# Revit family: AluStar Rondo
name_source: partatom
category: HLS-Bauteile
revit_build: Autodesk Revit 2018 (Build: 20170223_1515(x64)
units: mm (PartAtom-declared; Revit-internal decimal feet)

## family parameters
Basisbauteil = Wand
Beim Laden mit Abzugskörper schneiden = Nein
Bemaßung runder Anschluss = Durchmesser verwenden
Gemeinsam genutzt = Nein
Immer vertikal = Ja
Raumberechnungspunkt = Nein
Teiletyp = Normal

## types (6) — shared parameters
Rohbauöffnung = Ja
T1 = 13.5 mm
T2 = 39 mm
T_plate = 1.5 mm  [stored 0.00492126 ft]

## per-type parameters (varying)
| type | B | B1 | B2_Max | B2_min | B3 | B4 | B5 | BLock | Binner | Bz | Di | Din | HAN | Vb | Vh |
| Gipskarton12.5 - D200 | 200 mm  [stored 0.656168 ft] | 200 mm  [stored 0.656168 ft] | 217 mm | 202 mm | 257 mm | 197 mm | 194 mm | 98.5 mm | 28.5 mm | 300 mm | 192.5 mm | 143 mm | 21377 | 21.5 mm | 21.5 mm |
| Gipskarton12.5 - D300 | 300 mm | 300 mm | 317 mm | 302 mm | 357 mm | 297 mm | 294 mm | 148.5 mm | 28.5 mm | 400 mm | 292.5 mm | 243 mm | 21379 | 21.5 mm | 21.5 mm |
| Gipskarton12.5 - D400 | 400 mm | 400 mm | 417 mm | 402 mm | 457 mm | 397 mm | 394 mm | 198.5 mm | 28.5 mm | 500 mm | 392.5 mm | 343 mm | 21380 | 21.5 mm | 21.5 mm |
| Gipskarton12.5 - D500 | 500 mm | 494 mm | 517 mm | 502 mm | 544 mm | 488 mm | 486 mm | 244 mm  [stored 0.800525 ft] | 25 mm  [stored 0.082021 ft] | 600 mm | 484.5 mm | 444 mm | 21381 | 28 mm | 28 mm |
| Gipskarton12.5 - D600 | 600 mm | 600 mm | 617 mm | 602 mm | 657 mm | 597 mm | 594 mm | 298.5 mm | 28.5 mm | 700 mm | 592.5 mm | 543 mm | 21382 | 21.5 mm | 21.5 mm |
| Gipskarton12.5 - D250 | 250 mm | 250 mm | 267 mm | 252 mm | 307 mm  [stored 1.00722 ft] | 247 mm | 244 mm  [stored 0.800525 ft] | 123.5 mm | 28.5 mm | 350 mm  [stored 1.14829 ft] | 242.5 mm | 193 mm | 21378 | 21.5 mm | 21.5 mm |

note: [stored X ft] marks values corroborated as IEEE doubles in the binary element streams (Revit-internal decimal feet)
